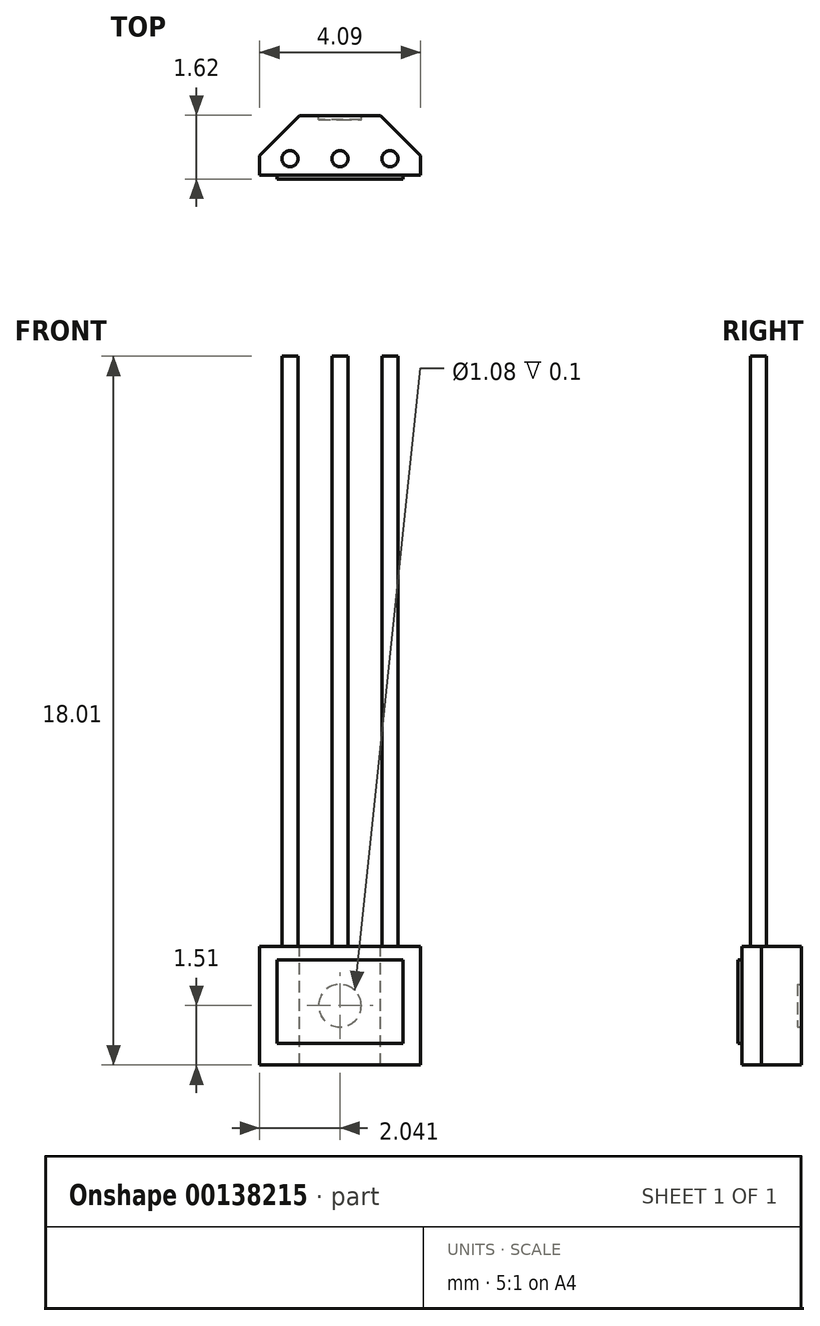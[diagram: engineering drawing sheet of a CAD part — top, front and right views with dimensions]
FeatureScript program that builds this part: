
annotation { "Feature Type Name" : "Feature", "Feature Type Description" : "" }
export const myFeature = defineFeature(function(context is Context, id is Id, definition is map)
    precondition{}
    {
        {
            var Q0;
            Q0=qCreatedBy(makeId("Top.planeOp"),FACE);
            var sketch = newSketch(context, id + "F0", { "sketchPlane" : qUnion([Q0])});
            skLineSegment(sketch, "E0", {"start": v(4.36, 30.73) * mm, "end": v(4.36, 30.23) * mm});
            skLineSegment(sketch, "E1", {"start": v(4.36, 30.23) * mm, "end": v(8.45, 30.23) * mm});
            skLineSegment(sketch, "E2", {"start": v(8.45, 30.23) * mm, "end": v(8.45, 30.73) * mm});
            skLineSegment(sketch, "E3", {"start": v(8.45, 30.73) * mm, "end": v(7.43, 31.75) * mm});
            skLineSegment(sketch, "E4", {"start": v(7.43, 31.75) * mm, "end": v(5.38, 31.75) * mm});
            skLineSegment(sketch, "E5", {"start": v(5.38, 31.75) * mm, "end": v(4.36, 30.73) * mm});
            skLineSegment(sketch, "E6", {"start": v(6.4, 31.75) * mm, "end": v(6.4, 30.23) * mm, "construction": true});
            skSolve(sketch);
        }
        {
            var Q0;
            Q0 = qSketchRegion(id + "F0", true);
            extrude(context, id + "F1", {"entities" : qUnion([Q0]), "oppositeDirection" : true, "depth" : 3.02 * mm});
        }
        {
            var Q0;
            Q0=makeQuery(id+"F1.opExtrude","CAP_FACE",FACE,{"disambiguationData":[OSD([sQuery(id+"F0.wireOp",EDGE,"E0"),sQuery(id+"F0.wireOp",EDGE,"E1"),sQuery(id+"F0.wireOp",EDGE,"E2"),sQuery(id+"F0.wireOp",EDGE,"E3"),sQuery(id+"F0.wireOp",EDGE,"E4"),sQuery(id+"F0.wireOp",EDGE,"E5")])],"isStart":true});
            var sketch = newSketch(context, id + "F2", { "sketchPlane" : qUnion([Q0])});
            skLineSegment(sketch, "E7", {"start": v(6.4, 31.75) * mm, "end": v(6.4, 30.23) * mm, "construction": true});
            skCircle(sketch, "E8", {"center": v(6.4, 30.65) * mm, "radius": 0.2 * mm});
            skLineSegment(sketch, "E9", {"start": v(6.4, 30.65) * mm, "end": v(8.2, 30.65) * mm});
            skLineSegment(sketch, "E10", {"start": v(6.4, 30.65) * mm, "end": v(4.67, 30.65) * mm});
            skCircle(sketch, "E11", {"center": v(5.13, 30.65) * mm, "radius": 0.2 * mm});
            skCircle(sketch, "E12", {"center": v(7.67, 30.65) * mm, "radius": 0.2 * mm});
            skSolve(sketch);
        }
        {
            var Q0;
            Q0 = qSketchRegion(id + "F2", true);
            extrude(context, id + "F3", {"entities" : qUnion([Q0]), "depth" : 15 * mm});
        }
        {
            var Q0;
            Q0=makeQuery(id+"F1.opExtrude","SWEPT_FACE",FACE,{"disambiguationData":[OSD([sQuery(id+"F0.wireOp",EDGE,"E4")])]});
            var sketch = newSketch(context, id + "F4", { "sketchPlane" : qUnion([Q0])});
            skLineSegment(sketch, "E13", {"start": v(-6.4, -3.02) * mm, "end": v(-6.4, 0) * mm, "construction": true});
            skLineSegment(sketch, "E14", {"start": v(-7.43, -1.51) * mm, "end": v(-5.38, -1.51) * mm, "construction": true});
            skCircle(sketch, "E15", {"center": v(-6.4, -1.51) * mm, "radius": 0.54 * mm});
            skSolve(sketch);
        }
        {
            var Q0;
            Q0 = qSketchRegion(id + "F4", true);
            extrude(context, id + "F5", {"entities" : qUnion([Q0]), "operationType" : NewBodyOperationType.REMOVE, "oppositeDirection" : true, "depth" : .1 * mm});
        }
        {
            var Q0;
            Q0=makeQuery(id+"F1.opExtrude","SWEPT_FACE",FACE,{"disambiguationData":[OSD([sQuery(id+"F0.wireOp",EDGE,"E1")])]});
            var sketch = newSketch(context, id + "F6", { "sketchPlane" : qUnion([Q0])});
            skLineSegment(sketch, "E16.bottom", {"start": v(4.8, -2.47) * mm, "end": v(8, -2.47) * mm});
            skLineSegment(sketch, "E16.top", {"start": v(4.8, -0.35) * mm, "end": v(8, -0.35) * mm});
            skLineSegment(sketch, "E16.left", {"start": v(4.8, -2.47) * mm, "end": v(4.8, -0.35) * mm});
            skLineSegment(sketch, "E16.right", {"start": v(8, -2.47) * mm, "end": v(8, -0.35) * mm});
            skPoint(sketch, "E16.middle", {"position": v(6.4, -1.41) * mm});
            skPoint(sketch, "E16.middle.positionSnap0", {"position": v(6.4, -3.02) * mm});
            skPoint(sketch, "E16.centerSnap0", {"position": v(6.4, -3.02) * mm});
            skSolve(sketch);
        }
        {
            var Q0;
            Q0 = qSketchRegion(id + "F6", true);
            extrude(context, id + "F7", {"entities" : qUnion([Q0]), "operationType" : NewBodyOperationType.ADD, "depth" : .1 * mm});
        }
    });
